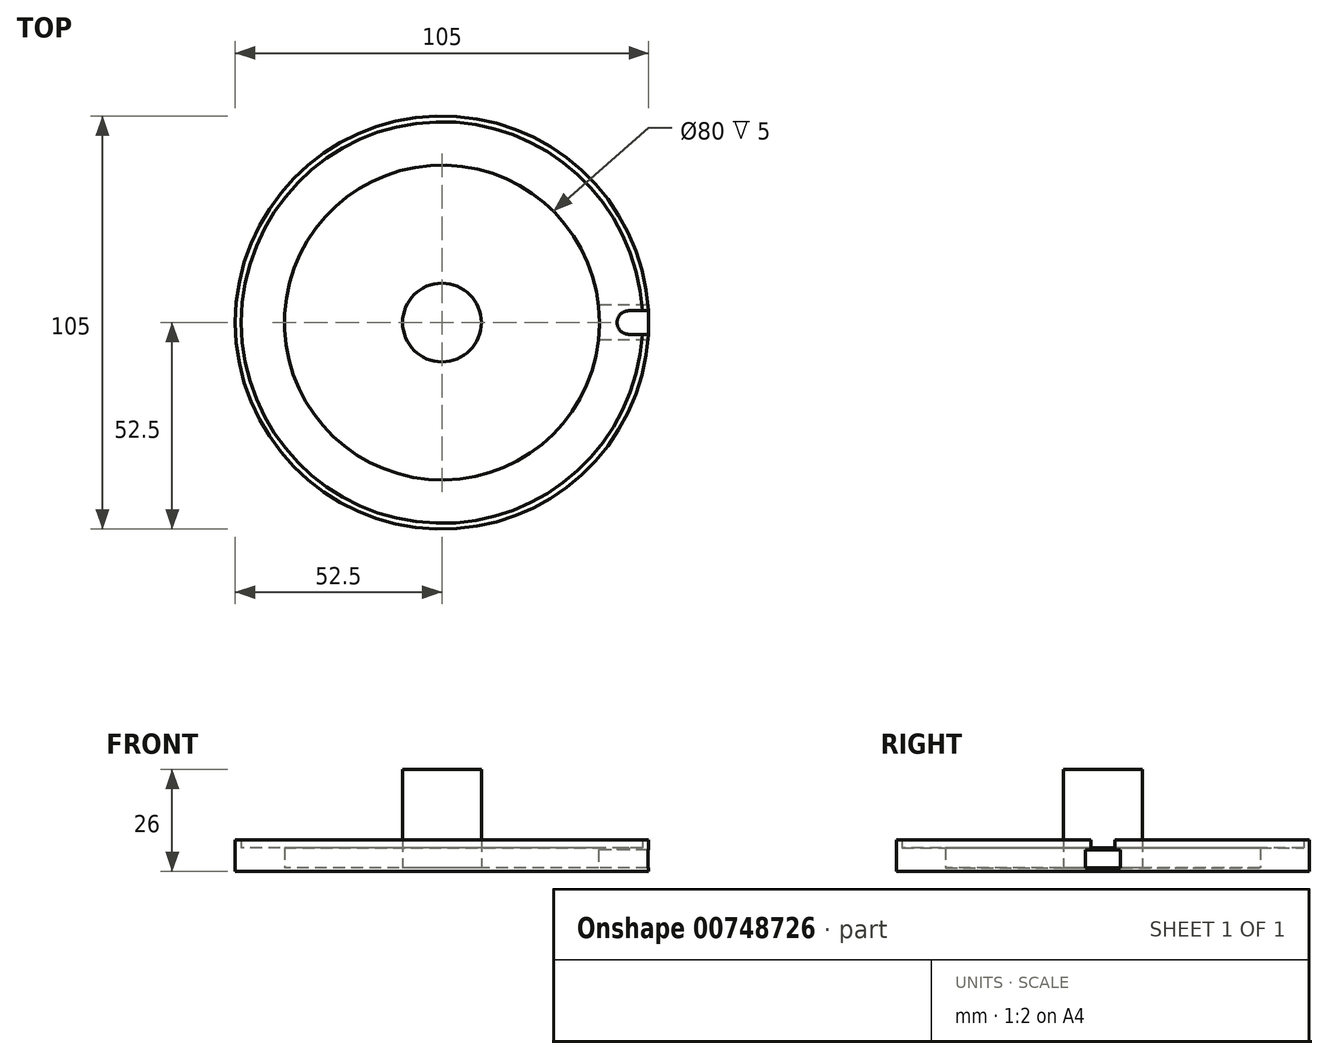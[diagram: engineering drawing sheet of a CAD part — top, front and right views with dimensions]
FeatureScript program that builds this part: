
annotation { "Feature Type Name" : "Feature", "Feature Type Description" : "" }
export const myFeature = defineFeature(function(context is Context, id is Id, definition is map)
    precondition{}
    {
        {
            var Q0;
            Q0=qCreatedBy(makeId("Top.planeOp"),FACE);
            var sketch = newSketch(context, id + "F0", { "sketchPlane" : qUnion([Q0])});
            skCircle(sketch, "E0", {"center": v(0, 0) * mm, "radius": 51 * mm});
            skCircle(sketch, "E1", {"center": v(0, 0) * mm, "radius": 40 * mm});
            skCircle(sketch, "E2", {"center": v(0, 0) * mm, "radius": 52.5 * mm});
            skSolve(sketch);
        }
        {
            var Q0;
            Q0=makeQuery(id+"F0.imprint","IMPRINT",FACE,{"disambiguationData":[TD([[makeQuery(id+"F0.imprint","IMPRINT",EDGE,{"derivedFrom":sQuery(id+"F0.wireOp",EDGE,"E1")}),1.0]])]});
            var Q1;
            Q1=makeQuery(id+"F0.imprint","IMPRINT",FACE,{"disambiguationData":[TD([[makeQuery(id+"F0.imprint","IMPRINT",EDGE,{"derivedFrom":sQuery(id+"F0.wireOp",EDGE,"E0")}),1.0]])]});
            var Q2;
            Q2=makeQuery(id+"F0.imprint","IMPRINT",FACE,{"disambiguationData":[TD([[makeQuery(id+"F0.imprint","IMPRINT",EDGE,{"derivedFrom":sQuery(id+"F0.wireOp",EDGE,"E0")}),-1.0]])]});
            extrude(context, id + "F1", {"entities" : qUnion([Q0, Q1, Q2]), "depth" : -1 * mm, "offsetDistance" : 25 * mm});
        }
        {
            var Q0;
            Q0=makeQuery(id+"F0.imprint","IMPRINT",FACE,{"disambiguationData":[TD([[makeQuery(id+"F0.imprint","IMPRINT",EDGE,{"derivedFrom":sQuery(id+"F0.wireOp",EDGE,"E0")}),1.0]])]});
            extrude(context, id + "F2", {"entities" : qUnion([Q0]), "operationType" : NewBodyOperationType.ADD, "depth" : 5 * mm, "offsetDistance" : 25 * mm});
        }
        {
            var Q0;
            Q0 = qSketchRegion(id + "F0", true);
            extrude(context, id + "F3", {"entities" : qUnion([Q0]), "operationType" : NewBodyOperationType.ADD, "depth" : 7 * mm, "offsetDistance" : 25 * mm});
        }
        {
            var Q0;
            Q0=qCreatedBy(makeId("Top.planeOp"),FACE);
            var sketch = newSketch(context, id + "F4", { "sketchPlane" : qUnion([Q0])});
            skLineSegment(sketch, "E3.bottom", {"start": v(55, -4.5) * mm, "end": v(35, -4.5) * mm});
            skLineSegment(sketch, "E3.top", {"start": v(55, 4.5) * mm, "end": v(35, 4.5) * mm});
            skLineSegment(sketch, "E3.left", {"start": v(55, -4.5) * mm, "end": v(55, 4.5) * mm});
            skLineSegment(sketch, "E3.right", {"start": v(35, -4.5) * mm, "end": v(35, 4.5) * mm});
            skPoint(sketch, "E3.middle", {"position": v(45, 0) * mm});
            skSolve(sketch);
        }
        {
            var Q0;
            Q0 = qSketchRegion(id + "F4", true);
            extrude(context, id + "F5", {"entities" : qUnion([Q0]), "operationType" : NewBodyOperationType.REMOVE, "depth" : 4.5 * mm, "offsetDistance" : 25 * mm});
        }
        {
            var Q0;
            Q0=qCreatedBy(makeId("Top.planeOp"),FACE);
            var sketch = newSketch(context, id + "F6", { "sketchPlane" : qUnion([Q0])});
            skCircle(sketch, "E4", {"center": v(47.5, 0) * mm, "radius": 3 * mm});
            skSolve(sketch);
        }
        {
            var Q0;
            Q0 = qSketchRegion(id + "F6", true);
            extrude(context, id + "F7", {"entities" : qUnion([Q0]), "operationType" : NewBodyOperationType.REMOVE, "endBound" : BoundingType.THROUGH_ALL, "depth" : 25 * mm, "offsetDistance" : 25 * mm});
        }
        {
            var Q0;
            Q0=qCreatedBy(makeId("Top.planeOp"),FACE);
            var sketch = newSketch(context, id + "F8", { "sketchPlane" : qUnion([Q0])});
            skLineSegment(sketch, "E5.bottom", {"start": v(47.55, 3) * mm, "end": v(55.6, 3) * mm});
            skLineSegment(sketch, "E5.top", {"start": v(47.55, -3) * mm, "end": v(55.6, -3) * mm});
            skLineSegment(sketch, "E5.left", {"start": v(47.55, 3) * mm, "end": v(47.55, -3) * mm});
            skLineSegment(sketch, "E5.right", {"start": v(55.6, 3) * mm, "end": v(55.6, -3) * mm});
            skPoint(sketch, "E5.middle", {"position": v(51.58, 0) * mm});
            skSolve(sketch);
        }
        {
            var Q0;
            Q0 = qSketchRegion(id + "F8", true);
            extrude(context, id + "F9", {"entities" : qUnion([Q0]), "operationType" : NewBodyOperationType.REMOVE, "depth" : 10 * mm, "offsetDistance" : 25 * mm});
        }
        {
            var Q0;
            Q0=makeQuery(id+"F0.imprint","IMPRINT",FACE,{"disambiguationData":[TD([[makeQuery(id+"F0.imprint","IMPRINT",EDGE,{"derivedFrom":sQuery(id+"F0.wireOp",EDGE,"E1")}),1.0]])]});
            var sketch = newSketch(context, id + "F10", { "sketchPlane" : qUnion([Q0])});
            skCircle(sketch, "E6", {"center": v(0, 0) * mm, "radius": 10 * mm});
            skSolve(sketch);
        }
        {
            var Q0;
            Q0 = qSketchRegion(id + "F10", true);
            extrude(context, id + "F11", {"entities" : qUnion([Q0]), "operationType" : NewBodyOperationType.ADD, "depth" : 25 * mm, "offsetDistance" : 25 * mm});
        }
    });
